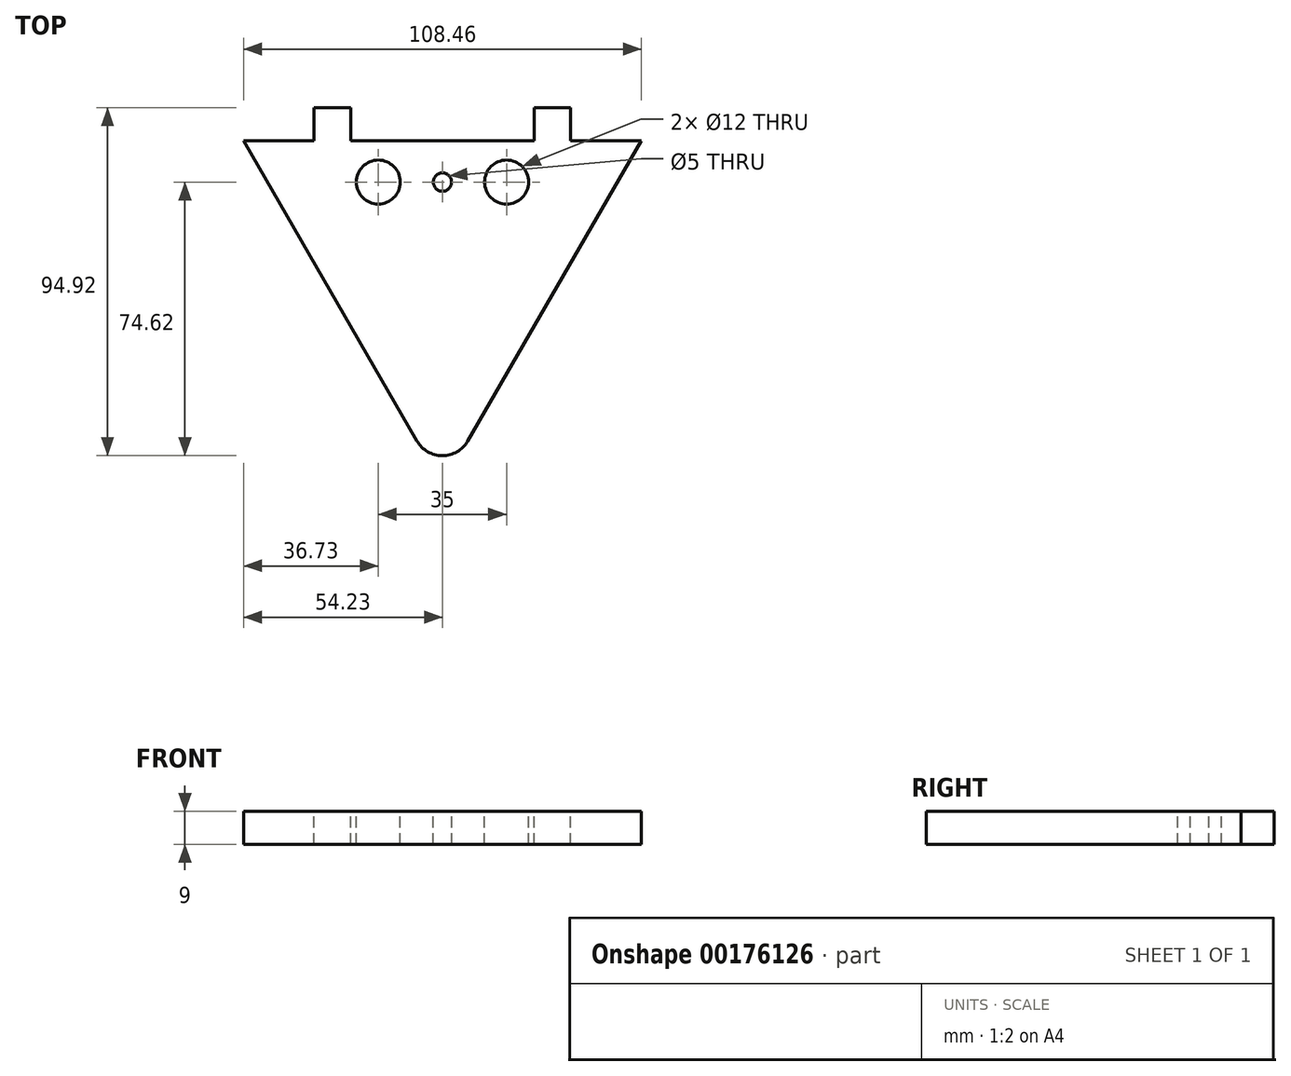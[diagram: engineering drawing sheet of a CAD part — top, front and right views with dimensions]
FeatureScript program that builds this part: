
annotation { "Feature Type Name" : "Feature", "Feature Type Description" : "" }
export const myFeature = defineFeature(function(context is Context, id is Id, definition is map)
    precondition{}
    {
        {
            var Q0;
            Q0=qCreatedBy(makeId("Top.planeOp"),FACE);
            var sketch = newSketch(context, id + "F0", { "sketchPlane" : qUnion([Q0])});
            skCircle(sketch, "E0.cCircle", {"center": v(0, 0) * mm, "radius": 34.64 * mm, "construction": true});
            skLineSegment(sketch, "E0.0", {"start": v(-60, 34.64) * mm, "end": v(60, 34.64) * mm});
            skLineSegment(sketch, "E0.1", {"start": v(60, 34.64) * mm, "end": v(0, -69.28) * mm});
            skLineSegment(sketch, "E0.2", {"start": v(0, -69.28) * mm, "end": v(-60, 34.64) * mm});
            skPoint(sketch, "E0.0.midPoint", {"position": v(0, 34.64) * mm});
            skSolve(sketch);
        }
        {
            var Q0;
            Q0 = qSketchRegion(id + "F0", true);
            extrude(context, id + "F1", {"entities" : qUnion([Q0]), "depth" : 9 * mm});
        }
        {
            var Q0;
            Q0=makeQuery(id+"F1.opExtrude","SWEPT_EDGE",EDGE,{"disambiguationData":[OSD([sQuery(id+"F0.wireOp",EDGE,"E0.1"),sQuery(id+"F0.wireOp",EDGE,"E0.2")])]});
            fillet(context, id + "F2", {"entities" : qUnion([Q0]), "radius" : 8 * mm, "tangentPropagation" : true, "allowEdgeOverflow" : false});
        }
        {
            var Q0;
            Q0=makeQuery(id+"F1.opExtrude","CAP_FACE",FACE,{"disambiguationData":[OSD([sQuery(id+"F0.wireOp",EDGE,"E0.0"),sQuery(id+"F0.wireOp",EDGE,"E0.1"),sQuery(id+"F0.wireOp",EDGE,"E0.2")])],"isStart":false});
            var sketch = newSketch(context, id + "F3", { "sketchPlane" : qUnion([Q0])});
            skLineSegment(sketch, "E1.0", {"start": v(40.47, 22.82) * mm, "end": v(7.4, -34.46) * mm});
            skLineSegment(sketch, "E2.0", {"start": v(-25.2, -3.62) * mm, "end": v(-58.28, 53.66) * mm});
            skCircle(sketch, "E3", {"center": v(17.5, 13.34) * mm, "radius": 6 * mm});
            skCircle(sketch, "E4", {"center": v(-17.5, 13.34) * mm, "radius": 6 * mm});
            skLineSegment(sketch, "E5", {"start": v(-35, 13.34) * mm, "end": v(35, 13.34) * mm});
            skLineSegment(sketch, "E6", {"start": v(0, 13.34) * mm, "end": v(35, 13.34) * mm});
            skLineSegment(sketch, "E7", {"start": v(0, 13.34) * mm, "end": v(-35, 13.34) * mm});
            skSolve(sketch);
        }
        {
            var Q0;
            Q0 = qSketchRegion(id + "F3", true);
            extrude(context, id + "F4", {"entities" : qUnion([Q0]), "operationType" : NewBodyOperationType.REMOVE, "oppositeDirection" : true, "depth" : 25 * mm});
        }
        {
            var Q0;
            Q0=makeQuery(id+"F1.opExtrude","SWEPT_FACE",FACE,{"disambiguationData":[OSD([sQuery(id+"F0.wireOp",EDGE,"E0.0")])]});
            var sketch = newSketch(context, id + "F5", { "sketchPlane" : qUnion([Q0])});
            skLineSegment(sketch, "E8.bottom", {"start": v(-60, 0) * mm, "end": v(60, 0) * mm});
            skLineSegment(sketch, "E8.top", {"start": v(-60, 9) * mm, "end": v(60, 9) * mm});
            skLineSegment(sketch, "E8.left", {"start": v(-60, 0) * mm, "end": v(-60, 9) * mm});
            skLineSegment(sketch, "E8.right", {"start": v(60, 0) * mm, "end": v(60, 9) * mm});
            skSolve(sketch);
        }
        {
            var Q0;
            Q0=makeQuery(id+"F5.imprint","IMPRINT",FACE,{"disambiguationData":[TD([[makeQuery(id+"F5.imprint","IMPRINT",EDGE,{"derivedFrom":sQuery(id+"F5.wireOp",EDGE,"E8.bottom")}),-1.0]])]});
            extrude(context, id + "F6", {"entities" : qUnion([Q0]), "operationType" : NewBodyOperationType.REMOVE, "oppositeDirection" : true, "depth" : 10 * mm});
        }
        {
            var Q0;
            Q0=makeQuery(id+"F6.boolean.opBoolean","COPY",FACE,{"derivedFrom":makeQuery(id+"F6.opExtrude","CAP_FACE",FACE,{"disambiguationData":[OSD([sQuery(id+"F5.wireOp",EDGE,"E8.bottom"),sQuery(id+"F5.wireOp",EDGE,"E8.top"),sQuery(id+"F5.wireOp",EDGE,"E8.left"),sQuery(id+"F5.wireOp",EDGE,"E8.right")])],"isStart":false})});
            var sketch = newSketch(context, id + "F7", { "sketchPlane" : qUnion([Q0])});
            skLineSegment(sketch, "E9", {"start": v(0, 0) * mm, "end": v(25, 0) * mm});
            skLineSegment(sketch, "E10", {"start": v(0, 0) * mm, "end": v(-25, 0) * mm});
            skLineSegment(sketch, "E11.bottom", {"start": v(-25, 0) * mm, "end": v(-35, 0) * mm});
            skLineSegment(sketch, "E11.top", {"start": v(-25, 9) * mm, "end": v(-35, 9) * mm});
            skLineSegment(sketch, "E11.left", {"start": v(-25, 0) * mm, "end": v(-25, 9) * mm});
            skLineSegment(sketch, "E11.right", {"start": v(-35, 0) * mm, "end": v(-35, 9) * mm});
            skLineSegment(sketch, "E12.bottom", {"start": v(25, 0) * mm, "end": v(35, 0) * mm});
            skLineSegment(sketch, "E12.top", {"start": v(25, 9) * mm, "end": v(35, 9) * mm});
            skLineSegment(sketch, "E12.left", {"start": v(25, 0) * mm, "end": v(25, 9) * mm});
            skLineSegment(sketch, "E12.right", {"start": v(35, 0) * mm, "end": v(35, 9) * mm});
            skSolve(sketch);
        }
        {
            var Q0;
            Q0=makeQuery(id+"F7.imprint","IMPRINT",FACE,{"disambiguationData":[TD([[makeQuery(id+"F7.imprint","IMPRINT",EDGE,{"derivedFrom":sQuery(id+"F7.wireOp",EDGE,"E11.bottom")}),-1.0]])]});
            var Q1;
            Q1=makeQuery(id+"F7.imprint","IMPRINT",FACE,{"disambiguationData":[TD([[makeQuery(id+"F7.imprint","IMPRINT",EDGE,{"derivedFrom":sQuery(id+"F7.wireOp",EDGE,"E12.bottom")}),-1.0]])]});
            extrude(context, id + "F8", {"entities" : qUnion([Q0, Q1]), "operationType" : NewBodyOperationType.ADD, "depth" : 9 * mm});
        }
        {
            var Q0;
            Q0=makeQuery(id+"F8.boolean.opBoolean","MERGE",FACE,{"derivedFrom":[makeQuery(id+"F1.opExtrude","CAP_FACE",FACE,{"disambiguationData":[OSD([sQuery(id+"F0.wireOp",EDGE,"E0.0"),sQuery(id+"F0.wireOp",EDGE,"E0.1"),sQuery(id+"F0.wireOp",EDGE,"E0.2")])],"isStart":false}),makeQuery(id+"F8.opExtrude","SWEPT_FACE",FACE,{"disambiguationData":[OSD([sQuery(id+"F7.wireOp",EDGE,"E11.top")])]}),makeQuery(id+"F8.opExtrude","SWEPT_FACE",FACE,{"disambiguationData":[OSD([sQuery(id+"F7.wireOp",EDGE,"E12.top")])]})]});
            var sketch = newSketch(context, id + "F9", { "sketchPlane" : qUnion([Q0])});
            skLineSegment(sketch, "E13", {"start": v(-17.5, 13.34) * mm, "end": v(17.5, 13.34) * mm});
            skCircle(sketch, "E14", {"center": v(0, 13.34) * mm, "radius": 2.5 * mm});
            skSolve(sketch);
        }
        {
            var Q0;
            {var subQ0=sQuery(id+"F9.wireOp",EDGE,"E14");var subQ1=sQuery(id+"F9.wireOp",EDGE,"E13");var subQ2=makeQuery(id+"F9.imprint","INTERSECT",VERTEX,{"disambiguationData":[OD(0.0)],"derivedFrom":[subQ1,subQ0]});Q0=makeQuery(id+"F9.imprint","IMPRINT",FACE,{"disambiguationData":[TD([[makeQuery(id+"F9.imprint","IMPRINT",EDGE,{"disambiguationData":[TD([[subQ2,-1.0]])],"derivedFrom":subQ1}),1.0]])]});}
            var Q1;
            {var subQ0=sQuery(id+"F9.wireOp",EDGE,"E14");var subQ1=sQuery(id+"F9.wireOp",EDGE,"E13");var subQ2=makeQuery(id+"F9.imprint","INTERSECT",VERTEX,{"disambiguationData":[OD(0.0)],"derivedFrom":[subQ1,subQ0]});Q1=makeQuery(id+"F9.imprint","IMPRINT",FACE,{"disambiguationData":[TD([[makeQuery(id+"F9.imprint","IMPRINT",EDGE,{"disambiguationData":[TD([[subQ2,-1.0]])],"derivedFrom":subQ1}),-1.0]])]});}
            extrude(context, id + "F10", {"entities" : qUnion([Q0, Q1]), "operationType" : NewBodyOperationType.REMOVE, "oppositeDirection" : true, "depth" : 25 * mm});
        }
    });
